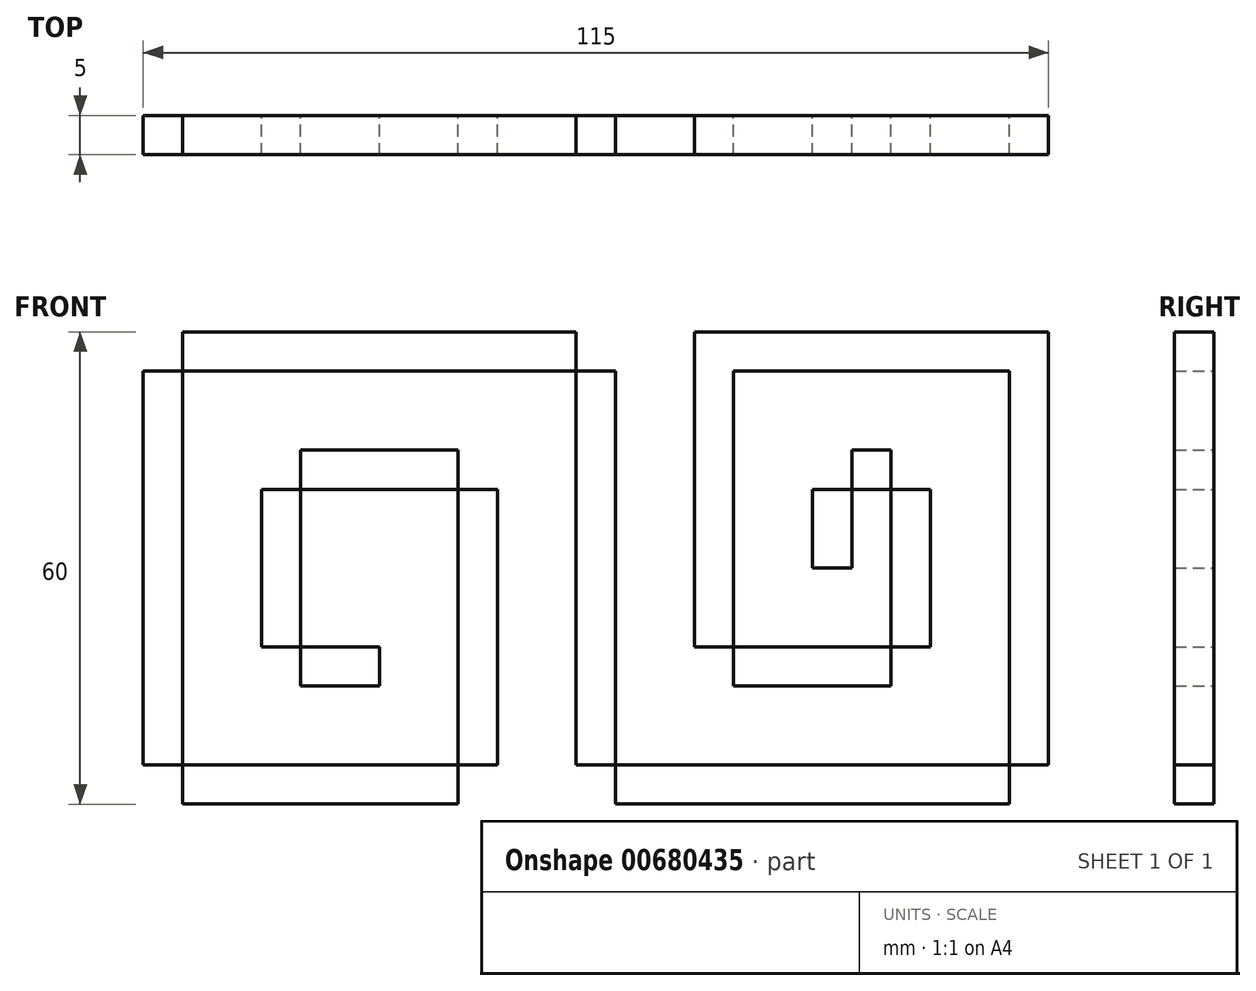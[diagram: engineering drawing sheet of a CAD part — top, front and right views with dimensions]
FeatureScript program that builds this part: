
annotation { "Feature Type Name" : "Feature", "Feature Type Description" : "" }
export const myFeature = defineFeature(function(context is Context, id is Id, definition is map)
    precondition{}
    {
        {
            var Q0;
            Q0=qCreatedBy(makeId("Front.planeOp"),FACE);
            var sketch = newSketch(context, id + "F0", { "sketchPlane" : qUnion([Q0])});
            skLineSegment(sketch, "E0.bottom", {"start": v(-51.18, 33.43) * mm, "end": v(-6.18, 33.43) * mm});
            skLineSegment(sketch, "E0.top", {"start": v(-51.18, 28.43) * mm, "end": v(-6.18, 28.43) * mm});
            skLineSegment(sketch, "E0.left", {"start": v(-51.18, 33.43) * mm, "end": v(-51.18, 28.43) * mm});
            skLineSegment(sketch, "E0.right", {"start": v(-6.18, 33.43) * mm, "end": v(-6.18, 28.43) * mm});
            skLineSegment(sketch, "E1.bottom", {"start": v(-6.18, 33.43) * mm, "end": v(-11.18, 33.43) * mm});
            skLineSegment(sketch, "E1.top", {"start": v(-6.18, -26.57) * mm, "end": v(-11.18, -26.57) * mm});
            skLineSegment(sketch, "E1.left", {"start": v(-6.18, 33.43) * mm, "end": v(-6.18, -26.57) * mm});
            skLineSegment(sketch, "E1.right", {"start": v(-11.18, 33.43) * mm, "end": v(-11.18, -26.57) * mm});
            skLineSegment(sketch, "E2.bottom", {"start": v(-6.18, -26.57) * mm, "end": v(-66.18, -26.57) * mm});
            skLineSegment(sketch, "E2.top", {"start": v(-6.18, -21.57) * mm, "end": v(-66.18, -21.57) * mm});
            skLineSegment(sketch, "E2.left", {"start": v(-6.18, -26.57) * mm, "end": v(-6.18, -21.57) * mm});
            skLineSegment(sketch, "E2.right", {"start": v(-66.18, -26.57) * mm, "end": v(-66.18, -21.57) * mm});
            skLineSegment(sketch, "E3.bottom", {"start": v(-66.18, -26.57) * mm, "end": v(-61.18, -26.57) * mm});
            skLineSegment(sketch, "E3.top", {"start": v(-66.18, 33.43) * mm, "end": v(-61.18, 33.43) * mm});
            skLineSegment(sketch, "E3.left", {"start": v(-66.18, -26.57) * mm, "end": v(-66.18, 33.43) * mm});
            skLineSegment(sketch, "E3.right", {"start": v(-61.18, -26.57) * mm, "end": v(-61.18, 33.43) * mm});
            skLineSegment(sketch, "E4.bottom", {"start": v(-51.18, 33.43) * mm, "end": v(-46.18, 33.43) * mm});
            skLineSegment(sketch, "E4.top", {"start": v(-51.18, -11.57) * mm, "end": v(-46.18, -11.57) * mm});
            skLineSegment(sketch, "E4.left", {"start": v(-51.18, 33.43) * mm, "end": v(-51.18, -11.57) * mm});
            skLineSegment(sketch, "E4.right", {"start": v(-46.18, 33.43) * mm, "end": v(-46.18, -11.57) * mm});
            skLineSegment(sketch, "E5.bottom", {"start": v(-51.18, -11.57) * mm, "end": v(-21.18, -11.57) * mm});
            skLineSegment(sketch, "E5.top", {"start": v(-51.18, -6.57) * mm, "end": v(-21.18, -6.57) * mm});
            skLineSegment(sketch, "E5.left", {"start": v(-51.18, -11.57) * mm, "end": v(-51.18, -6.57) * mm});
            skLineSegment(sketch, "E5.right", {"start": v(-21.18, -11.57) * mm, "end": v(-21.18, -6.57) * mm});
            skLineSegment(sketch, "E6.bottom", {"start": v(-21.18, -11.57) * mm, "end": v(-26.18, -11.57) * mm});
            skLineSegment(sketch, "E6.top", {"start": v(-21.18, 18.43) * mm, "end": v(-26.18, 18.43) * mm});
            skLineSegment(sketch, "E6.left", {"start": v(-21.18, -11.57) * mm, "end": v(-21.18, 18.43) * mm});
            skLineSegment(sketch, "E6.right", {"start": v(-26.18, -11.57) * mm, "end": v(-26.18, 18.43) * mm});
            skLineSegment(sketch, "E7.bottom", {"start": v(-21.18, 18.43) * mm, "end": v(-36.18, 18.43) * mm});
            skLineSegment(sketch, "E7.top", {"start": v(-21.18, 13.43) * mm, "end": v(-36.18, 13.43) * mm});
            skLineSegment(sketch, "E7.left", {"start": v(-21.18, 18.43) * mm, "end": v(-21.18, 13.43) * mm});
            skLineSegment(sketch, "E7.right", {"start": v(-36.18, 18.43) * mm, "end": v(-36.18, 13.43) * mm});
            skLineSegment(sketch, "E8.bottom", {"start": v(-36.18, 18.43) * mm, "end": v(-31.18, 18.43) * mm});
            skLineSegment(sketch, "E8.top", {"start": v(-36.18, 3.43) * mm, "end": v(-31.18, 3.43) * mm});
            skLineSegment(sketch, "E8.left", {"start": v(-36.18, 18.43) * mm, "end": v(-36.18, 3.43) * mm});
            skLineSegment(sketch, "E8.right", {"start": v(-31.18, 18.43) * mm, "end": v(-31.18, 3.43) * mm});
            skLineSegment(sketch, "E9.bottom", {"start": v(-61.18, 33.43) * mm, "end": v(-121.18, 33.43) * mm});
            skLineSegment(sketch, "E9.top", {"start": v(-61.18, 28.43) * mm, "end": v(-121.18, 28.43) * mm});
            skLineSegment(sketch, "E9.left", {"start": v(-61.18, 33.43) * mm, "end": v(-61.18, 28.43) * mm});
            skLineSegment(sketch, "E9.right", {"start": v(-121.18, 33.43) * mm, "end": v(-121.18, 28.43) * mm});
            skLineSegment(sketch, "E10.bottom", {"start": v(-121.18, 33.43) * mm, "end": v(-116.18, 33.43) * mm});
            skLineSegment(sketch, "E10.top", {"start": v(-121.18, -26.57) * mm, "end": v(-116.18, -26.57) * mm});
            skLineSegment(sketch, "E10.left", {"start": v(-121.18, 33.43) * mm, "end": v(-121.18, -26.57) * mm});
            skLineSegment(sketch, "E10.right", {"start": v(-116.18, 33.43) * mm, "end": v(-116.18, -26.57) * mm});
            skLineSegment(sketch, "E11.bottom", {"start": v(-121.18, -26.57) * mm, "end": v(-76.18, -26.57) * mm});
            skLineSegment(sketch, "E11.top", {"start": v(-121.18, -21.57) * mm, "end": v(-76.18, -21.57) * mm});
            skLineSegment(sketch, "E11.left", {"start": v(-121.18, -26.57) * mm, "end": v(-121.18, -21.57) * mm});
            skLineSegment(sketch, "E11.right", {"start": v(-76.18, -26.57) * mm, "end": v(-76.18, -21.57) * mm});
            skLineSegment(sketch, "E12.bottom", {"start": v(-76.18, -26.57) * mm, "end": v(-81.18, -26.57) * mm});
            skLineSegment(sketch, "E12.top", {"start": v(-76.18, 18.43) * mm, "end": v(-81.18, 18.43) * mm});
            skLineSegment(sketch, "E12.left", {"start": v(-76.18, -26.57) * mm, "end": v(-76.18, 18.43) * mm});
            skLineSegment(sketch, "E12.right", {"start": v(-81.18, -26.57) * mm, "end": v(-81.18, 18.43) * mm});
            skLineSegment(sketch, "E13.bottom", {"start": v(-76.18, 18.43) * mm, "end": v(-106.18, 18.43) * mm});
            skLineSegment(sketch, "E13.top", {"start": v(-76.18, 13.43) * mm, "end": v(-106.18, 13.43) * mm});
            skLineSegment(sketch, "E13.left", {"start": v(-76.18, 18.43) * mm, "end": v(-76.18, 13.43) * mm});
            skLineSegment(sketch, "E13.right", {"start": v(-106.18, 18.43) * mm, "end": v(-106.18, 13.43) * mm});
            skLineSegment(sketch, "E14.bottom", {"start": v(-106.18, 18.43) * mm, "end": v(-101.18, 18.43) * mm});
            skLineSegment(sketch, "E14.top", {"start": v(-106.18, -11.57) * mm, "end": v(-101.18, -11.57) * mm});
            skLineSegment(sketch, "E14.left", {"start": v(-106.18, 18.43) * mm, "end": v(-106.18, -11.57) * mm});
            skLineSegment(sketch, "E14.right", {"start": v(-101.18, 18.43) * mm, "end": v(-101.18, -11.57) * mm});
            skLineSegment(sketch, "E15.bottom", {"start": v(-106.18, -11.57) * mm, "end": v(-91.18, -11.57) * mm});
            skLineSegment(sketch, "E15.top", {"start": v(-106.18, -6.57) * mm, "end": v(-91.18, -6.57) * mm});
            skLineSegment(sketch, "E15.left", {"start": v(-106.18, -11.57) * mm, "end": v(-106.18, -6.57) * mm});
            skLineSegment(sketch, "E15.right", {"start": v(-91.18, -11.57) * mm, "end": v(-91.18, -6.57) * mm});
            skSolve(sketch);
        }
        {
            var Q0;
            {var subQ0=sQuery(id+"F0.wireOp",EDGE,"E14.left");var subQ1=sQuery(id+"F0.wireOp",EDGE,"E13.top");var subQ2=makeQuery(id+"F0.imprint","INTERSECT",VERTEX,{"derivedFrom":[subQ1,subQ0]});Q0=makeQuery(id+"F0.imprint","IMPRINT",FACE,{"disambiguationData":[TD([[makeQuery(id+"F0.imprint","IMPRINT",EDGE,{"disambiguationData":[TD([[subQ2,1.0]])],"derivedFrom":subQ1}),1.0]])]});}
            var Q1;
            {var subQ0=sQuery(id+"F0.wireOp",EDGE,"E6.left");var subQ1=sQuery(id+"F0.wireOp",EDGE,"E5.top");var subQ2=makeQuery(id+"F0.imprint","INTERSECT",VERTEX,{"derivedFrom":[subQ1,subQ0]});Q1=makeQuery(id+"F0.imprint","IMPRINT",FACE,{"disambiguationData":[TD([[makeQuery(id+"F0.imprint","IMPRINT",EDGE,{"disambiguationData":[TD([[subQ2,1.0]])],"derivedFrom":subQ1}),1.0]])]});}
            var Q2;
            {var subQ0=sQuery(id+"F0.wireOp",EDGE,"E7.bottom");var subQ1=sQuery(id+"F0.wireOp",EDGE,"E6.right");var subQ2=makeQuery(id+"F0.imprint","INTERSECT",VERTEX,{"derivedFrom":[subQ1,subQ0]});Q2=makeQuery(id+"F0.imprint","IMPRINT",FACE,{"disambiguationData":[TD([[makeQuery(id+"F0.imprint","IMPRINT",EDGE,{"disambiguationData":[TD([[subQ2,1.0]])],"derivedFrom":subQ1}),1.0]])]});}
            var Q3;
            {var subQ0=sQuery(id+"F0.wireOp",EDGE,"E11.bottom");var subQ1=sQuery(id+"F0.wireOp",EDGE,"E10.right");var subQ2=makeQuery(id+"F0.imprint","INTERSECT",VERTEX,{"derivedFrom":[subQ1,subQ0]});Q3=makeQuery(id+"F0.imprint","IMPRINT",FACE,{"disambiguationData":[TD([[makeQuery(id+"F0.imprint","IMPRINT",EDGE,{"disambiguationData":[TD([[subQ2,1.0]])],"derivedFrom":subQ1}),1.0]])]});}
            var Q4;
            {var subQ0=sQuery(id+"F0.wireOp",EDGE,"E5.bottom");var subQ1=sQuery(id+"F0.wireOp",EDGE,"E4.right");var subQ2=makeQuery(id+"F0.imprint","INTERSECT",VERTEX,{"derivedFrom":[subQ1,subQ0]});Q4=makeQuery(id+"F0.imprint","IMPRINT",FACE,{"disambiguationData":[TD([[makeQuery(id+"F0.imprint","IMPRINT",EDGE,{"disambiguationData":[TD([[subQ2,1.0]])],"derivedFrom":subQ1}),1.0]])]});}
            var Q5;
            {var subQ5=sQuery(id+"F0.wireOp",EDGE,"E15.right");Q5=makeQuery(id+"F0.imprint","IMPRINT",FACE,{"disambiguationData":[TD([[makeQuery(id+"F0.imprint","IMPRINT",EDGE,{"derivedFrom":subQ5}),1.0]])]});}
            var Q6;
            {var subQ5=sQuery(id+"F0.wireOp",EDGE,"E8.top");Q6=makeQuery(id+"F0.imprint","IMPRINT",FACE,{"disambiguationData":[TD([[makeQuery(id+"F0.imprint","IMPRINT",EDGE,{"derivedFrom":subQ5}),1.0]])]});}
            var Q7;
            {var subQ0=sQuery(id+"F0.wireOp",EDGE,"E0.bottom");Q7=makeQuery(id+"F0.imprint","IMPRINT",FACE,{"disambiguationData":[TD([[makeQuery(id+"F0.imprint","IMPRINT",EDGE,{"derivedFrom":subQ0}),-1.0]])]});}
            var Q8;
            {var subQ0=sQuery(id+"F0.wireOp",EDGE,"E9.bottom");var subQ1=sQuery(id+"F0.wireOp",EDGE,"E3.left");var subQ2=makeQuery(id+"F0.imprint","INTERSECT",VERTEX,{"derivedFrom":[subQ1,subQ0]});Q8=makeQuery(id+"F0.imprint","IMPRINT",FACE,{"disambiguationData":[TD([[makeQuery(id+"F0.imprint","IMPRINT",EDGE,{"disambiguationData":[TD([[subQ2,1.0]])],"derivedFrom":subQ1}),1.0]])]});}
            var Q9;
            {var subQ0=sQuery(id+"F0.wireOp",EDGE,"E4.left");var subQ1=sQuery(id+"F0.wireOp",EDGE,"E0.top");var subQ2=makeQuery(id+"F0.imprint","INTERSECT",VERTEX,{"derivedFrom":[subQ1,subQ0]});Q9=makeQuery(id+"F0.imprint","IMPRINT",FACE,{"disambiguationData":[TD([[makeQuery(id+"F0.imprint","IMPRINT",EDGE,{"disambiguationData":[TD([[subQ2,-1.0]])],"derivedFrom":subQ1}),-1.0]])]});}
            var Q10;
            {var subQ0=sQuery(id+"F0.wireOp",EDGE,"E13.bottom");var subQ1=sQuery(id+"F0.wireOp",EDGE,"E12.right");var subQ2=makeQuery(id+"F0.imprint","INTERSECT",VERTEX,{"derivedFrom":[subQ1,subQ0]});Q10=makeQuery(id+"F0.imprint","IMPRINT",FACE,{"disambiguationData":[TD([[makeQuery(id+"F0.imprint","IMPRINT",EDGE,{"disambiguationData":[TD([[subQ2,1.0]])],"derivedFrom":subQ1}),1.0]])]});}
            var Q11;
            {var subQ0=sQuery(id+"F0.wireOp",EDGE,"E2.bottom");var subQ1=sQuery(id+"F0.wireOp",EDGE,"E1.right");var subQ2=makeQuery(id+"F0.imprint","INTERSECT",VERTEX,{"derivedFrom":[subQ1,subQ0]});Q11=makeQuery(id+"F0.imprint","IMPRINT",FACE,{"disambiguationData":[TD([[makeQuery(id+"F0.imprint","IMPRINT",EDGE,{"disambiguationData":[TD([[subQ2,1.0]])],"derivedFrom":subQ1}),-1.0]])]});}
            var Q12;
            {var subQ0=sQuery(id+"F0.wireOp",EDGE,"E10.left");var subQ1=sQuery(id+"F0.wireOp",EDGE,"E9.top");var subQ2=makeQuery(id+"F0.imprint","INTERSECT",VERTEX,{"derivedFrom":[subQ1,subQ0]});Q12=makeQuery(id+"F0.imprint","IMPRINT",FACE,{"disambiguationData":[TD([[makeQuery(id+"F0.imprint","IMPRINT",EDGE,{"disambiguationData":[TD([[subQ2,1.0]])],"derivedFrom":subQ1}),1.0]])]});}
            var Q13;
            {var subQ0=sQuery(id+"F0.wireOp",EDGE,"E1.left");var subQ1=sQuery(id+"F0.wireOp",EDGE,"E0.top");var subQ2=makeQuery(id+"F0.imprint","INTERSECT",VERTEX,{"derivedFrom":[subQ1,subQ0]});Q13=makeQuery(id+"F0.imprint","IMPRINT",FACE,{"disambiguationData":[TD([[makeQuery(id+"F0.imprint","IMPRINT",EDGE,{"disambiguationData":[TD([[subQ2,1.0]])],"derivedFrom":subQ1}),-1.0]])]});}
            var Q14;
            {var subQ0=sQuery(id+"F0.wireOp",EDGE,"E12.left");var subQ1=sQuery(id+"F0.wireOp",EDGE,"E11.top");var subQ2=makeQuery(id+"F0.imprint","INTERSECT",VERTEX,{"derivedFrom":[subQ1,subQ0]});Q14=makeQuery(id+"F0.imprint","IMPRINT",FACE,{"disambiguationData":[TD([[makeQuery(id+"F0.imprint","IMPRINT",EDGE,{"disambiguationData":[TD([[subQ2,1.0]])],"derivedFrom":subQ1}),1.0]])]});}
            var Q15;
            {var subQ5=sQuery(id+"F0.wireOp",EDGE,"E8.bottom");Q15=makeQuery(id+"F0.imprint","IMPRINT",FACE,{"disambiguationData":[TD([[makeQuery(id+"F0.imprint","IMPRINT",EDGE,{"derivedFrom":subQ5}),-1.0]])]});}
            var Q16;
            {var subQ0=sQuery(id+"F0.wireOp",EDGE,"E3.left");var subQ1=sQuery(id+"F0.wireOp",EDGE,"E2.top");var subQ2=makeQuery(id+"F0.imprint","INTERSECT",VERTEX,{"derivedFrom":[subQ1,subQ0]});Q16=makeQuery(id+"F0.imprint","IMPRINT",FACE,{"disambiguationData":[TD([[makeQuery(id+"F0.imprint","IMPRINT",EDGE,{"disambiguationData":[TD([[subQ2,1.0]])],"derivedFrom":subQ1}),-1.0]])]});}
            var Q17;
            {var subQ5=sQuery(id+"F0.wireOp",EDGE,"E7.left");Q17=makeQuery(id+"F0.imprint","IMPRINT",FACE,{"disambiguationData":[TD([[makeQuery(id+"F0.imprint","IMPRINT",EDGE,{"derivedFrom":subQ5}),-1.0]])]});}
            var Q18;
            {var subQ5=sQuery(id+"F0.wireOp",EDGE,"E5.left");Q18=makeQuery(id+"F0.imprint","IMPRINT",FACE,{"disambiguationData":[TD([[makeQuery(id+"F0.imprint","IMPRINT",EDGE,{"derivedFrom":subQ5}),-1.0]])]});}
            var Q19;
            {var subQ5=sQuery(id+"F0.wireOp",EDGE,"E1.bottom");Q19=makeQuery(id+"F0.imprint","IMPRINT",FACE,{"disambiguationData":[TD([[makeQuery(id+"F0.imprint","IMPRINT",EDGE,{"derivedFrom":subQ5}),1.0]])]});}
            var Q20;
            {var subQ5=sQuery(id+"F0.wireOp",EDGE,"E6.bottom");Q20=makeQuery(id+"F0.imprint","IMPRINT",FACE,{"disambiguationData":[TD([[makeQuery(id+"F0.imprint","IMPRINT",EDGE,{"derivedFrom":subQ5}),-1.0]])]});}
            var Q21;
            {var subQ5=sQuery(id+"F0.wireOp",EDGE,"E15.left");Q21=makeQuery(id+"F0.imprint","IMPRINT",FACE,{"disambiguationData":[TD([[makeQuery(id+"F0.imprint","IMPRINT",EDGE,{"derivedFrom":subQ5}),-1.0]])]});}
            var Q22;
            {var subQ5=sQuery(id+"F0.wireOp",EDGE,"E14.bottom");Q22=makeQuery(id+"F0.imprint","IMPRINT",FACE,{"disambiguationData":[TD([[makeQuery(id+"F0.imprint","IMPRINT",EDGE,{"derivedFrom":subQ5}),-1.0]])]});}
            var Q23;
            {var subQ5=sQuery(id+"F0.wireOp",EDGE,"E13.left");Q23=makeQuery(id+"F0.imprint","IMPRINT",FACE,{"disambiguationData":[TD([[makeQuery(id+"F0.imprint","IMPRINT",EDGE,{"derivedFrom":subQ5}),-1.0]])]});}
            var Q24;
            {var subQ5=sQuery(id+"F0.wireOp",EDGE,"E10.bottom");Q24=makeQuery(id+"F0.imprint","IMPRINT",FACE,{"disambiguationData":[TD([[makeQuery(id+"F0.imprint","IMPRINT",EDGE,{"derivedFrom":subQ5}),-1.0]])]});}
            var Q25;
            {var subQ5=sQuery(id+"F0.wireOp",EDGE,"E11.left");Q25=makeQuery(id+"F0.imprint","IMPRINT",FACE,{"disambiguationData":[TD([[makeQuery(id+"F0.imprint","IMPRINT",EDGE,{"derivedFrom":subQ5}),-1.0]])]});}
            var Q26;
            {var subQ5=sQuery(id+"F0.wireOp",EDGE,"E2.left");Q26=makeQuery(id+"F0.imprint","IMPRINT",FACE,{"disambiguationData":[TD([[makeQuery(id+"F0.imprint","IMPRINT",EDGE,{"derivedFrom":subQ5}),1.0]])]});}
            var Q27;
            {var subQ5=sQuery(id+"F0.wireOp",EDGE,"E4.bottom");Q27=makeQuery(id+"F0.imprint","IMPRINT",FACE,{"disambiguationData":[TD([[makeQuery(id+"F0.imprint","IMPRINT",EDGE,{"derivedFrom":subQ5}),-1.0]])]});}
            var Q28;
            {var subQ5=sQuery(id+"F0.wireOp",EDGE,"E9.left");Q28=makeQuery(id+"F0.imprint","IMPRINT",FACE,{"disambiguationData":[TD([[makeQuery(id+"F0.imprint","IMPRINT",EDGE,{"derivedFrom":subQ5}),-1.0]])]});}
            var Q29;
            {var subQ5=sQuery(id+"F0.wireOp",EDGE,"E12.bottom");Q29=makeQuery(id+"F0.imprint","IMPRINT",FACE,{"disambiguationData":[TD([[makeQuery(id+"F0.imprint","IMPRINT",EDGE,{"derivedFrom":subQ5}),-1.0]])]});}
            var Q30;
            {var subQ5=sQuery(id+"F0.wireOp",EDGE,"E3.bottom");Q30=makeQuery(id+"F0.imprint","IMPRINT",FACE,{"disambiguationData":[TD([[makeQuery(id+"F0.imprint","IMPRINT",EDGE,{"derivedFrom":subQ5}),1.0]])]});}
            extrude(context, id + "F1", {"entities" : qUnion([Q0, Q1, Q2, Q3, Q4, Q5, Q6, Q7, Q8, Q9, Q10, Q11, Q12, Q13, Q14, Q15, Q16, Q17, Q18, Q19, Q20, Q21, Q22, Q23, Q24, Q25, Q26, Q27, Q28, Q29, Q30]), "depth" : 5 * mm, "offsetDistance" : 25 * mm});
        }
    });
